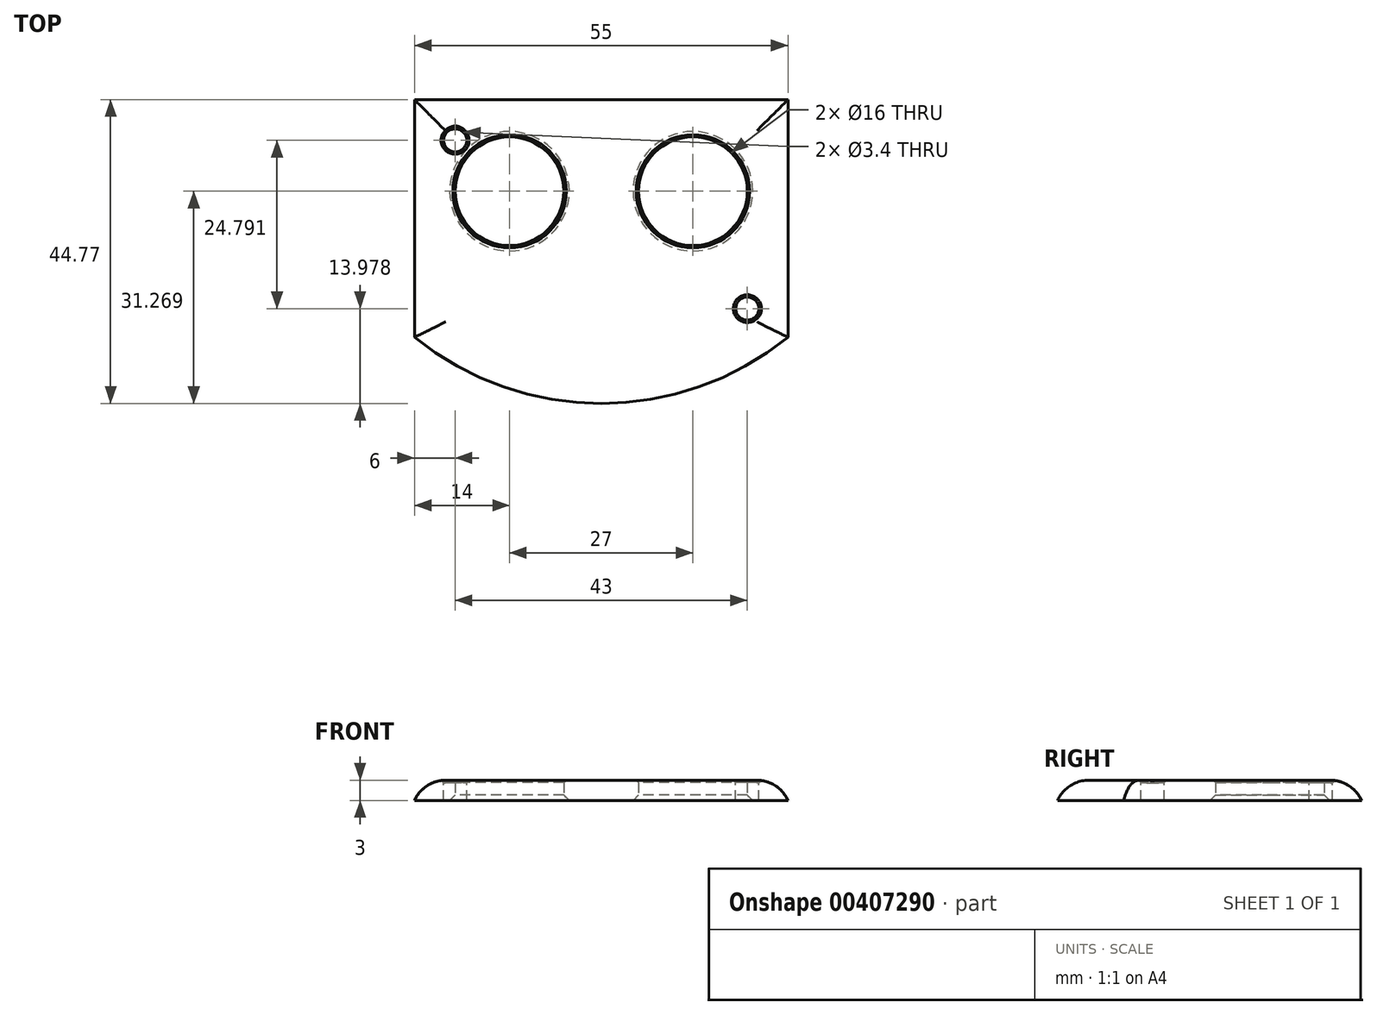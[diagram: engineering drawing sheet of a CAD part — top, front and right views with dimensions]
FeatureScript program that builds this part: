
annotation { "Feature Type Name" : "Feature", "Feature Type Description" : "" }
export const myFeature = defineFeature(function(context is Context, id is Id, definition is map)
    precondition{}
    {
        {
            var Q0;
            Q0=qCreatedBy(makeId("Top.planeOp"),FACE);
            var sketch = newSketch(context, id + "F0", { "sketchPlane" : qUnion([Q0])});
            skLineSegment(sketch, "E0", {"start": v(-13.75, 29.48) * mm, "end": v(-13.75, -5.52) * mm});
            skArc(sketch, "E1", {"start": v(-13.75, -5.52) * mm, "mid": v(13.75, -15.29) * mm, "end": v(41.25, -5.52) * mm});
            skLineSegment(sketch, "E2", {"start": v(-13.75, 29.48) * mm, "end": v(41.25, 29.48) * mm});
            skLineSegment(sketch, "E3", {"start": v(41.25, 29.48) * mm, "end": v(41.25, -5.52) * mm});
            skLineSegment(sketch, "E4", {"start": v(13.75, 29.48) * mm, "end": v(13.75, 15.98) * mm});
            skLineSegment(sketch, "E5", {"start": v(13.75, 15.98) * mm, "end": v(27.25, 15.98) * mm});
            skLineSegment(sketch, "E6.MirrorCS", {"start": v(13.75, 15.98) * mm, "end": v(0.25, 15.98) * mm});
            skCircle(sketch, "E7", {"center": v(0.25, 15.98) * mm, "radius": 8 * mm});
            skCircle(sketch, "E8", {"center": v(27.25, 15.98) * mm, "radius": 8 * mm});
            skSolve(sketch);
        }
        {
            var Q0;
            Q0 = qSketchRegion(id + "F0", true);
            extrude(context, id + "F1", {"entities" : qUnion([Q0]), "offsetDistance" : 25 * mm, "depth" : 3 * mm});
        }
        {
            var Q0;
            Q0=makeQuery(id+"F1.opExtrude","CAP_FACE",FACE,{"disambiguationData":[OSD([sQuery(id+"F0.wireOp",EDGE,"E0"),sQuery(id+"F0.wireOp",EDGE,"E1"),sQuery(id+"F0.wireOp",EDGE,"E2"),sQuery(id+"F0.wireOp",EDGE,"E3"),sQuery(id+"F0.wireOp",EDGE,"E7"),sQuery(id+"F0.wireOp",EDGE,"E8")])],"isStart":false});
            var sketch = newSketch(context, id + "F2", { "sketchPlane" : qUnion([Q0])});
            skLineSegment(sketch, "E9.top", {"start": v(-10.25, 20.98) * mm, "end": v(-5.25, 20.98) * mm});
            skLineSegment(sketch, "E9.right", {"start": v(-5.25, 25.98) * mm, "end": v(-5.25, 20.98) * mm});
            skCircle(sketch, "E10", {"center": v(-7.75, 23.48) * mm, "radius": 1.7 * mm});
            skPoint(sketch, "E10.centerSnap0", {"position": v(-5.25, 23.48) * mm});
            skPoint(sketch, "E10.centerSnap1", {"position": v(-7.75, 20.98) * mm});
            skLineSegment(sketch, "E11.bottom", {"start": v(-13.75, 29.48) * mm, "end": v(-5.25, 29.48) * mm});
            skLineSegment(sketch, "E11.top", {"start": v(-13.75, 20.98) * mm, "end": v(-5.25, 20.98) * mm});
            skLineSegment(sketch, "E11.left", {"start": v(-13.75, 29.48) * mm, "end": v(-13.75, 20.98) * mm});
            skLineSegment(sketch, "E11.right", {"start": v(-5.25, 29.48) * mm, "end": v(-5.25, 20.98) * mm});
            skLineSegment(sketch, "E12.top", {"start": v(37.75, 1.19) * mm, "end": v(32.75, 1.19) * mm});
            skLineSegment(sketch, "E12.right", {"start": v(32.75, -3.81) * mm, "end": v(32.75, 1.19) * mm});
            skLineSegment(sketch, "E13.bottom", {"start": v(32.75, 1.19) * mm, "end": v(38.88, 1.19) * mm});
            skLineSegment(sketch, "E13.left", {"start": v(32.75, 1.19) * mm, "end": v(32.75, -7.31) * mm});
            skCircle(sketch, "E14", {"center": v(35.25, -1.31) * mm, "radius": 1.7 * mm});
            skPoint(sketch, "E14.centerSnap0", {"position": v(35.25, 1.19) * mm});
            skPoint(sketch, "E14.centerSnap1", {"position": v(32.75, -1.31) * mm});
            skLineSegment(sketch, "E15", {"start": v(32.75, -7.31) * mm, "end": v(39.02, -5.84) * mm});
            skLineSegment(sketch, "E16", {"start": v(39.02, -5.84) * mm, "end": v(38.88, 1.19) * mm});
            skSolve(sketch);
        }
        {
            var Q0;
            Q0=makeQuery(id+"F2.imprint","IMPRINT",FACE,{"disambiguationData":[TD([[makeQuery(id+"F2.imprint","IMPRINT",EDGE,{"derivedFrom":sQuery(id+"F2.wireOp",EDGE,"E10")}),1.0]])]});
            var Q1;
            Q1=makeQuery(id+"F2.imprint","IMPRINT",FACE,{"disambiguationData":[TD([[makeQuery(id+"F2.imprint","IMPRINT",EDGE,{"derivedFrom":sQuery(id+"F2.wireOp",EDGE,"E14")}),1.0]])]});
            extrude(context, id + "F3", {"entities" : qUnion([Q0, Q1]), "operationType" : NewBodyOperationType.REMOVE, "oppositeDirection" : true, "depth" : 3 * mm});
        }
        {
            var Q0;
            Q0=makeQuery(id+"F1.opExtrude","CAP_EDGE",EDGE,{"disambiguationData":[OSD([sQuery(id+"F0.wireOp",EDGE,"E8")])],"isStart":true});
            var Q1;
            Q1=makeQuery(id+"F1.opExtrude","CAP_EDGE",EDGE,{"disambiguationData":[OSD([sQuery(id+"F0.wireOp",EDGE,"E7")])],"isStart":true});
            chamfer(context, id + "F4", {"entities" : qUnion([Q0, Q1]), "width" : 0.8 * mm, "tangentPropagation" : true});
        }
        {
            var Q0;
            Q0=makeQuery(id+"F1.opExtrude","CAP_EDGE",EDGE,{"disambiguationData":[OSD([sQuery(id+"F0.wireOp",EDGE,"E2")])],"isStart":false});
            var Q1;
            Q1=makeQuery(id+"F1.opExtrude","CAP_EDGE",EDGE,{"disambiguationData":[OSD([sQuery(id+"F0.wireOp",EDGE,"E0")])],"isStart":false});
            var Q2;
            Q2=makeQuery(id+"F1.opExtrude","CAP_EDGE",EDGE,{"disambiguationData":[OSD([sQuery(id+"F0.wireOp",EDGE,"E1")])],"isStart":false});
            var Q3;
            Q3=makeQuery(id+"F1.opExtrude","CAP_EDGE",EDGE,{"disambiguationData":[OSD([sQuery(id+"F0.wireOp",EDGE,"E3")])],"isStart":false});
            fillet(context, id + "F5", {"entities" : qUnion([Q0, Q1, Q2, Q3]), "radius" : 5 * mm, "tangentPropagation" : true, "defaultsChanged" : false, "vertexSettings" : [], "allowEdgeOverflow" : false});
        }
        {
            var Q0;
            {var subQ0=makeQuery(id+"F3.boolean.opBoolean","COPY",EDGE,{"derivedFrom":makeQuery(id+"F3.opExtrude","CAP_EDGE",EDGE,{"disambiguationData":[OSD([sQuery(id+"F2.wireOp",EDGE,"E10")])],"isStart":true})});Q0=qUnion([subQ0,subQ0]);}
            var Q1;
            Q1=makeQuery(id+"F5.opFillet","BLEND_EDGE",EDGE,{"blendedFrom":[makeQuery(id+"F1.opExtrude","CAP_EDGE",EDGE,{"disambiguationData":[OSD([sQuery(id+"F0.wireOp",EDGE,"E2")])],"isStart":false}),makeQuery(id+"F3.boolean.opBoolean","COPY",FACE,{"derivedFrom":makeQuery(id+"F3.opExtrude","SWEPT_FACE",FACE,{"disambiguationData":[OSD([sQuery(id+"F2.wireOp",EDGE,"E10")])]})})],"blendedInto":[makeQuery(id+"F3.boolean.opBoolean","COPY",FACE,{"derivedFrom":makeQuery(id+"F3.opExtrude","SWEPT_FACE",FACE,{"disambiguationData":[OSD([sQuery(id+"F2.wireOp",EDGE,"E10")])]})})]});
            var Q2;
            Q2=makeQuery(id+"F5.opFillet","BLEND_EDGE",EDGE,{"blendedFrom":[makeQuery(id+"F1.opExtrude","CAP_EDGE",EDGE,{"disambiguationData":[OSD([sQuery(id+"F0.wireOp",EDGE,"E0")])],"isStart":false}),makeQuery(id+"F3.boolean.opBoolean","COPY",FACE,{"derivedFrom":makeQuery(id+"F3.opExtrude","SWEPT_FACE",FACE,{"disambiguationData":[OSD([sQuery(id+"F2.wireOp",EDGE,"E10")])]})})],"blendedInto":[makeQuery(id+"F3.boolean.opBoolean","COPY",FACE,{"derivedFrom":makeQuery(id+"F3.opExtrude","SWEPT_FACE",FACE,{"disambiguationData":[OSD([sQuery(id+"F2.wireOp",EDGE,"E10")])]})})]});
            var Q3;
            Q3=makeQuery(id+"F5.opFillet","BLEND_EDGE",EDGE,{"blendedFrom":[makeQuery(id+"F1.opExtrude","CAP_EDGE",EDGE,{"disambiguationData":[OSD([sQuery(id+"F0.wireOp",EDGE,"E3")])],"isStart":false}),makeQuery(id+"F3.boolean.opBoolean","COPY",FACE,{"derivedFrom":makeQuery(id+"F3.opExtrude","SWEPT_FACE",FACE,{"disambiguationData":[OSD([sQuery(id+"F2.wireOp",EDGE,"E14")])]})})],"blendedInto":[makeQuery(id+"F3.boolean.opBoolean","COPY",FACE,{"derivedFrom":makeQuery(id+"F3.opExtrude","SWEPT_FACE",FACE,{"disambiguationData":[OSD([sQuery(id+"F2.wireOp",EDGE,"E14")])]})})]});
            var Q4;
            Q4=makeQuery(id+"F3.boolean.opBoolean","COPY",EDGE,{"derivedFrom":makeQuery(id+"F3.opExtrude","CAP_EDGE",EDGE,{"disambiguationData":[OSD([sQuery(id+"F2.wireOp",EDGE,"E14")])],"isStart":true})});
            var Q5;
            Q5=makeQuery(id+"F1.opExtrude","CAP_EDGE",EDGE,{"disambiguationData":[OSD([sQuery(id+"F0.wireOp",EDGE,"E7")])],"isStart":false});
            var Q6;
            Q6=makeQuery(id+"F1.opExtrude","CAP_EDGE",EDGE,{"disambiguationData":[OSD([sQuery(id+"F0.wireOp",EDGE,"E8")])],"isStart":false});
            chamfer(context, id + "F6", {"entities" : qUnion([Q0, Q1, Q2, Q3, Q4, Q5, Q6]), "width" : 0.35 * mm, "tangentPropagation" : true});
        }
    });
